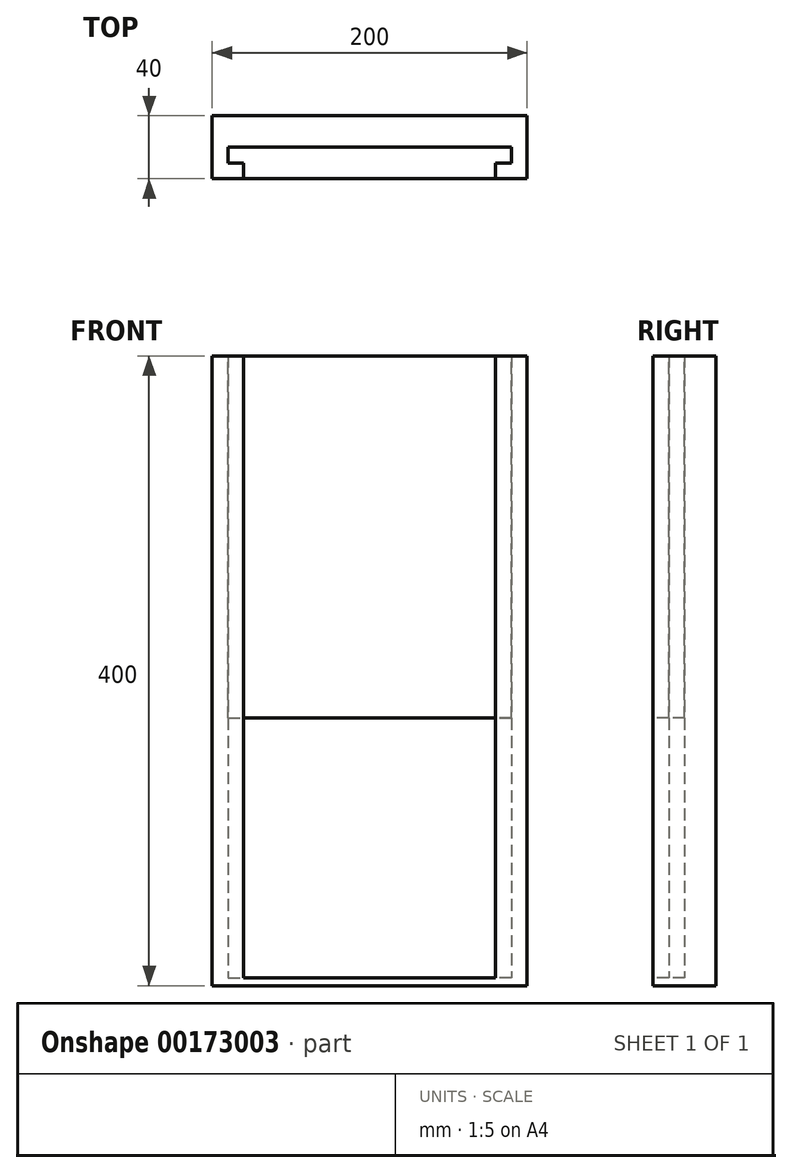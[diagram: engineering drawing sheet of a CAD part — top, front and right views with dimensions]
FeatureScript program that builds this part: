
annotation { "Feature Type Name" : "Feature", "Feature Type Description" : "" }
export const myFeature = defineFeature(function(context is Context, id is Id, definition is map)
    precondition{}
    {
        {
            var Q0;
            Q0=qCreatedBy(makeId("Top.planeOp"),FACE);
            var sketch = newSketch(context, id + "F0", { "sketchPlane" : qUnion([Q0])});
            skLineSegment(sketch, "E0", {"start": v(80, 0) * mm, "end": v(100, 0) * mm});
            skLineSegment(sketch, "E1", {"start": v(100, 0) * mm, "end": v(100, 40) * mm});
            skLineSegment(sketch, "E2", {"start": v(100, 40) * mm, "end": v(0, 40) * mm});
            skLineSegment(sketch, "E3", {"start": v(0, 40) * mm, "end": v(0, 20) * mm});
            skLineSegment(sketch, "E4", {"start": v(0, 20) * mm, "end": v(90, 20) * mm});
            skLineSegment(sketch, "E5", {"start": v(90, 20) * mm, "end": v(90, 10) * mm});
            skLineSegment(sketch, "E6", {"start": v(90, 10) * mm, "end": v(80, 10) * mm});
            skLineSegment(sketch, "E7", {"start": v(80, 10) * mm, "end": v(80, 0) * mm});
            skLineSegment(sketch, "E8", {"start": v(0, 40) * mm, "end": v(0, 0) * mm, "construction": true});
            skLineSegment(sketch, "E9.MirrorCS", {"start": v(-100, 40) * mm, "end": v(0, 40) * mm});
            skLineSegment(sketch, "E10.MirrorCS", {"start": v(0, 20) * mm, "end": v(-90, 20) * mm});
            skLineSegment(sketch, "E11.MirrorCS", {"start": v(-90, 20) * mm, "end": v(-90, 10) * mm});
            skLineSegment(sketch, "E12.MirrorCS", {"start": v(-90, 10) * mm, "end": v(-80, 10) * mm});
            skLineSegment(sketch, "E13.MirrorCS", {"start": v(-80, 10) * mm, "end": v(-80, 0) * mm});
            skLineSegment(sketch, "E14.MirrorCS", {"start": v(-80, 0) * mm, "end": v(-100, 0) * mm});
            skLineSegment(sketch, "E15.MirrorCS", {"start": v(-100, 0) * mm, "end": v(-100, 40) * mm});
            skSolve(sketch);
        }
        {
            var Q0;
            Q0 = qSketchRegion(id + "F0", true);
            extrude(context, id + "F1", {"entities" : qUnion([Q0]), "depth" : 280 * mm, "hasSecondDirection" : true, "secondDirectionOppositeDirection" : true, "secondDirectionDepth" : 120 * mm});
        }
        {
            var Q0;
            Q0=makeQuery(id+"F1.opExtrude","CAP_FACE",FACE,{"disambiguationData":[OSD([sQuery(id+"F0.wireOp",EDGE,"E0"),sQuery(id+"F0.wireOp",EDGE,"E1"),sQuery(id+"F0.wireOp",EDGE,"E2"),sQuery(id+"F0.wireOp",EDGE,"E4"),sQuery(id+"F0.wireOp",EDGE,"E5"),sQuery(id+"F0.wireOp",EDGE,"E6"),sQuery(id+"F0.wireOp",EDGE,"E7"),sQuery(id+"F0.wireOp",EDGE,"E9.MirrorCS"),sQuery(id+"F0.wireOp",EDGE,"E10.MirrorCS"),sQuery(id+"F0.wireOp",EDGE,"E11.MirrorCS"),sQuery(id+"F0.wireOp",EDGE,"E12.MirrorCS"),sQuery(id+"F0.wireOp",EDGE,"E13.MirrorCS"),sQuery(id+"F0.wireOp",EDGE,"E14.MirrorCS"),sQuery(id+"F0.wireOp",EDGE,"E15.MirrorCS")])],"isStart":false});
            var sketch = newSketch(context, id + "F2", { "sketchPlane" : qUnion([Q0])});
            skLineSegment(sketch, "E16", {"start": v(-80, 0) * mm, "end": v(-80, 10) * mm});
            skLineSegment(sketch, "E17", {"start": v(-80, 10) * mm, "end": v(-90, 10) * mm});
            skLineSegment(sketch, "E18", {"start": v(-90, 10) * mm, "end": v(-90, 20) * mm});
            skLineSegment(sketch, "E19", {"start": v(-90, 20) * mm, "end": v(90, 20) * mm});
            skLineSegment(sketch, "E20", {"start": v(90, 20) * mm, "end": v(90, 10) * mm});
            skLineSegment(sketch, "E21", {"start": v(90, 10) * mm, "end": v(80, 10) * mm});
            skLineSegment(sketch, "E22", {"start": v(80, 10) * mm, "end": v(80, 0) * mm});
            skLineSegment(sketch, "E23", {"start": v(80, 0) * mm, "end": v(-80, 0) * mm});
            skSolve(sketch);
        }
        {
            var Q0;
            Q0 = qSketchRegion(id + "F2", true);
            extrude(context, id + "F3", {"entities" : qUnion([Q0]), "oppositeDirection" : true, "depth" : 230 * mm});
        }
        {
            var Q0;
            Q0=makeQuery(id+"F1.opExtrude","CAP_FACE",FACE,{"disambiguationData":[OSD([sQuery(id+"F0.wireOp",EDGE,"E0"),sQuery(id+"F0.wireOp",EDGE,"E1"),sQuery(id+"F0.wireOp",EDGE,"E2"),sQuery(id+"F0.wireOp",EDGE,"E4"),sQuery(id+"F0.wireOp",EDGE,"E5"),sQuery(id+"F0.wireOp",EDGE,"E6"),sQuery(id+"F0.wireOp",EDGE,"E7"),sQuery(id+"F0.wireOp",EDGE,"E9.MirrorCS"),sQuery(id+"F0.wireOp",EDGE,"E10.MirrorCS"),sQuery(id+"F0.wireOp",EDGE,"E11.MirrorCS"),sQuery(id+"F0.wireOp",EDGE,"E12.MirrorCS"),sQuery(id+"F0.wireOp",EDGE,"E13.MirrorCS"),sQuery(id+"F0.wireOp",EDGE,"E14.MirrorCS"),sQuery(id+"F0.wireOp",EDGE,"E15.MirrorCS")])],"isStart":true});
            var sketch = newSketch(context, id + "F4", { "sketchPlane" : qUnion([Q0])});
            skLineSegment(sketch, "E24", {"start": v(-80, 0) * mm, "end": v(-80, -10) * mm});
            skLineSegment(sketch, "E25", {"start": v(-80, -10) * mm, "end": v(-90, -10) * mm});
            skLineSegment(sketch, "E26", {"start": v(-90, -10) * mm, "end": v(-90, -20) * mm});
            skLineSegment(sketch, "E27", {"start": v(-90, -20) * mm, "end": v(90, -20) * mm});
            skLineSegment(sketch, "E28", {"start": v(90, -20) * mm, "end": v(90, -10) * mm});
            skLineSegment(sketch, "E29", {"start": v(90, -10) * mm, "end": v(80, -10) * mm});
            skLineSegment(sketch, "E30", {"start": v(80, -10) * mm, "end": v(80, 0) * mm});
            skLineSegment(sketch, "E31", {"start": v(80, 0) * mm, "end": v(-80, 0) * mm});
            skSolve(sketch);
        }
        {
            var Q0;
            Q0 = qSketchRegion(id + "F4", true);
            extrude(context, id + "F5", {"entities" : qUnion([Q0]), "operationType" : NewBodyOperationType.ADD, "oppositeDirection" : true, "depth" : 5 * mm});
        }
    });
